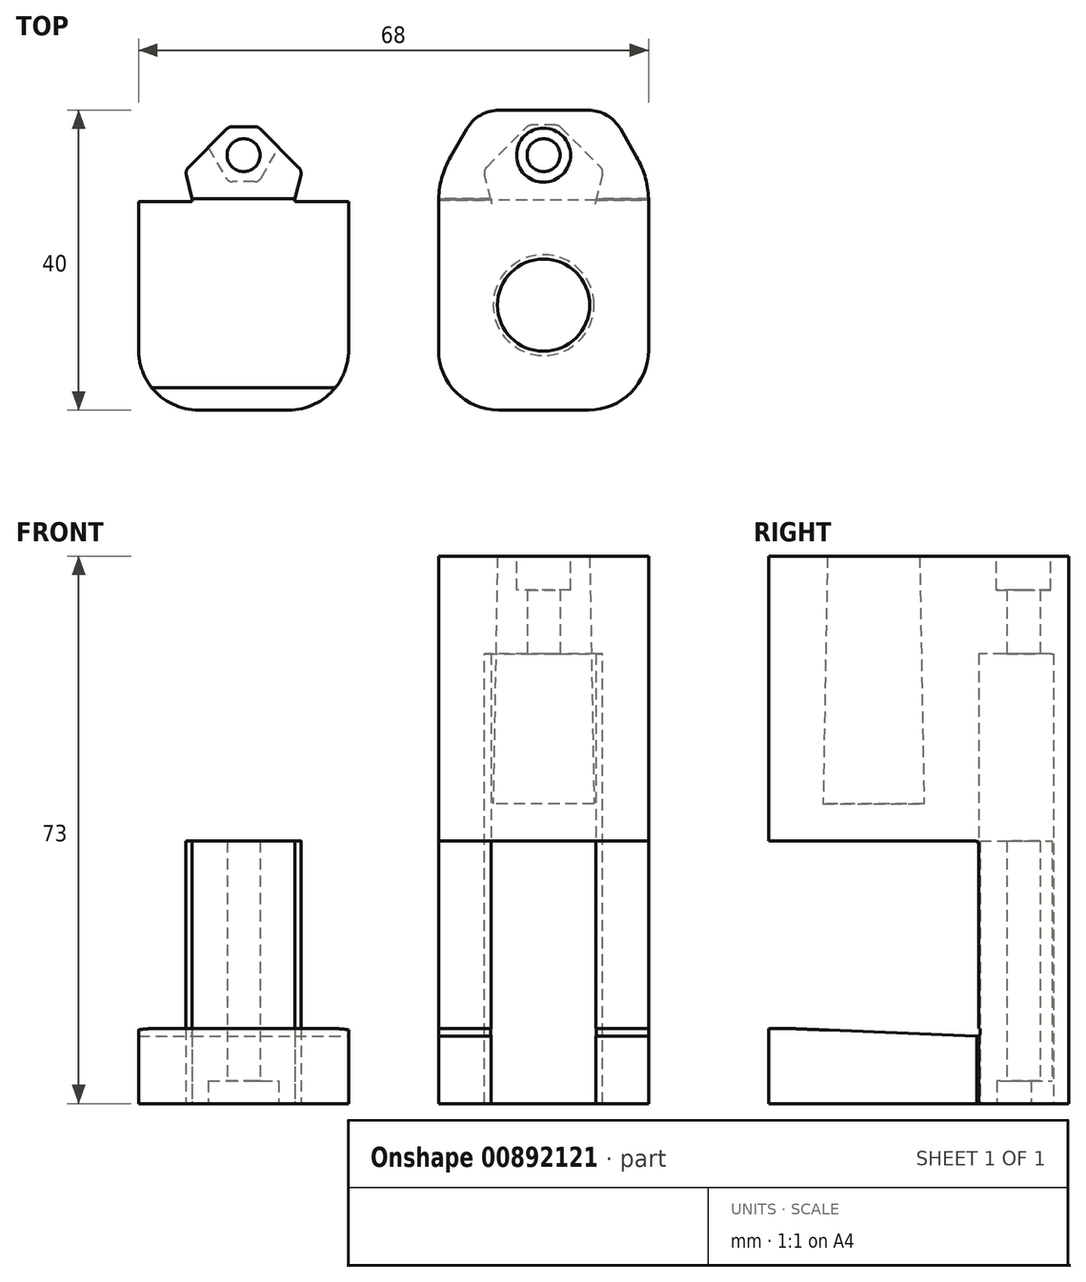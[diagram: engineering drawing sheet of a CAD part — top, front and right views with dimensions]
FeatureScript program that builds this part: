
annotation { "Feature Type Name" : "Feature", "Feature Type Description" : "" }
export const myFeature = defineFeature(function(context is Context, id is Id, definition is map)
    precondition{}
    {
        {
            assignVariable(context, id + "F0", {"name" : "lamppostDepth", "anyValue" : 33});
        }
        {
            var Q0;
            Q0=qCreatedBy(makeId("Right.planeOp"),FACE);
            var sketch = newSketch(context, id + "F1", { "sketchPlane" : qUnion([Q0])});
            skLineSegment(sketch, "E0", {"start": v(0, 0) * mm, "end": v(-28, 0) * mm});
            skLineSegment(sketch, "E1", {"start": v(-28, 0) * mm, "end": v(-28, 38) * mm});
            skLineSegment(sketch, "E2", {"start": v(-28, 38) * mm, "end": v(12, 38) * mm});
            skLineSegment(sketch, "E3", {"start": v(12, 38) * mm, "end": v(12, -35) * mm});
            skLineSegment(sketch, "E4", {"start": v(12, -35) * mm, "end": v(0, -35) * mm});
            skLineSegment(sketch, "E5", {"start": v(0, -35) * mm, "end": v(0, 0) * mm});
            skLineSegment(sketch, "E6", {"start": v(0, -25) * mm, "end": v(-22.92, -25) * mm, "construction": true});
            skSolve(sketch);
        }
        {
            var Q0;
            Q0=qSketchRegion(id+"F1",true);
            extrude(context, id + "F2", {"entities" : qUnion([Q0]), "endBound" : BoundingType.SYMMETRIC, "depth" : 28 * mm, "offsetDistance" : 25 * mm});
        }
        {
            var Q0;
            Q0=makeQuery(id+"F2.opExtrude","SWEPT_FACE",FACE,{"disambiguationData":[OSD([sQuery(id+"F1.wireOp",EDGE,"E2")])]});
            var sketch = newSketch(context, id + "F3", { "sketchPlane" : qUnion([Q0])});
            skCircle(sketch, "E7", {"center": v(0, -14) * mm, "radius": 6.15 * mm});
            skLineSegment(sketch, "E8", {"start": v(14, -28) * mm, "end": v(-14, 0) * mm, "construction": true});
            skLineSegment(sketch, "E9", {"start": v(-14, 0) * mm, "end": v(-14, -28) * mm, "construction": true});
            skSolve(sketch);
        }
        {
            var Q0;
            Q0=qSketchRegion(id+"F3",true);
            extrude(context, id + "F4", {"entities" : qUnion([Q0]), "operationType" : NewBodyOperationType.REMOVE, "oppositeDirection" : true, "depth" : (getVariable(context, 'lamppostDepth')) * mm, "offsetDistance" : 25 * mm, "hasDraft" : true, "draftAngle" : 1 * degree});
        }
        {
            var Q0;
            Q0=makeQuery(id+"F2.opExtrude","SWEPT_FACE",FACE,{"disambiguationData":[OSD([sQuery(id+"F1.wireOp",EDGE,"E4")])]});
            var sketch = newSketch(context, id + "F5", { "sketchPlane" : qUnion([Q0])});
            skCircle(sketch, "E10", {"center": v(0, -6) * mm, "radius": 2.2 * mm});
            skLineSegment(sketch, "E11", {"start": v(-14, -12) * mm, "end": v(14, 0) * mm, "construction": true});
            skSolve(sketch);
        }
        {
            var Q0;
            Q0=qSketchRegion(id+"F5",true);
            extrude(context, id + "F6", {"entities" : qUnion([Q0]), "operationType" : NewBodyOperationType.REMOVE, "endBound" : BoundingType.THROUGH_ALL, "oppositeDirection" : true, "depth" : 25 * mm, "offsetDistance" : 25 * mm});
        }
        {
            var Q0;
            Q0=makeQuery(id+"F2.opExtrude","SWEPT_FACE",FACE,{"disambiguationData":[OSD([sQuery(id+"F1.wireOp",EDGE,"E2")])]});
            var sketch = newSketch(context, id + "F7", { "sketchPlane" : qUnion([Q0])});
            skCircle(sketch, "E12", {"center": v(0, 6) * mm, "radius": 3.6 * mm});
            skSolve(sketch);
        }
        {
            var Q0;
            Q0=qSketchRegion(id+"F7",true);
            extrude(context, id + "F8", {"entities" : qUnion([Q0]), "operationType" : NewBodyOperationType.REMOVE, "oppositeDirection" : true, "depth" : 4.5 * mm, "offsetDistance" : 25 * mm});
        }
        {
            var Q0;
            Q0=makeQuery(id+"F2.opExtrude","SWEPT_FACE",FACE,{"disambiguationData":[OSD([sQuery(id+"F1.wireOp",EDGE,"E4")])]});
            var sketch = newSketch(context, id + "F9", { "sketchPlane" : qUnion([Q0])});
            skLineSegment(sketch, "E13", {"start": v(2, -10) * mm, "end": v(-2, -10) * mm});
            skPoint(sketch, "E14", {"position": v(0, -6) * mm});
            skLineSegment(sketch, "E15", {"start": v(0, -6) * mm, "end": v(0, -10) * mm, "construction": true});
            skLineSegment(sketch, "E16", {"start": v(2, -10) * mm, "end": v(8, -4) * mm});
            skLineSegment(sketch, "E17", {"start": v(8, -4) * mm, "end": v(7, 0) * mm});
            skLineSegment(sketch, "E18", {"start": v(7, 0) * mm, "end": v(-7, 0) * mm});
            skLineSegment(sketch, "E19", {"start": v(-7, 0) * mm, "end": v(-8, -4) * mm});
            skLineSegment(sketch, "E20", {"start": v(-8, -4) * mm, "end": v(-2, -10) * mm});
            skSolve(sketch);
        }
        {
            var Q0;
            Q0=qSketchRegion(id+"F9",true);
            extrude(context, id + "F10", {"entities" : qUnion([Q0]), "operationType" : NewBodyOperationType.REMOVE, "oppositeDirection" : true, "depth" : 60 * mm, "offsetDistance" : 25 * mm});
        }
        {
            var Q0;
            Q0=makeQuery(id+"F2.opExtrude","SWEPT_FACE",FACE,{"disambiguationData":[OSD([sQuery(id+"F1.wireOp",EDGE,"E4")])]});
            var sketch = newSketch(context, id + "F11", { "sketchPlane" : qUnion([Q0])});
            skLineSegment(sketch, "E21.0", {"start": v(7.78, -3.94) * mm, "end": v(6.84, -0.2) * mm});
            skLineSegment(sketch, "E21.1", {"start": v(-6.84, -0.2) * mm, "end": v(-7.78, -3.94) * mm});
            skLineSegment(sketch, "E21.2", {"start": v(-7.78, -3.94) * mm, "end": v(-1.92, -9.8) * mm});
            skLineSegment(sketch, "E21.3", {"start": v(1.92, -9.8) * mm, "end": v(-1.92, -9.8) * mm});
            skLineSegment(sketch, "E21.4", {"start": v(1.92, -9.8) * mm, "end": v(7.78, -3.94) * mm});
            skLineSegment(sketch, "E22", {"start": v(6.84, -0.2) * mm, "end": v(-6.84, -0.2) * mm});
            skCircle(sketch, "E23.0", {"center": v(0, -6) * mm, "radius": 2.2 * mm});
            skSolve(sketch);
        }
        {
            var Q0;
            Q0=qSketchRegion(id+"F11",true);
            extrude(context, id + "F12", {"entities" : qUnion([Q0]), "oppositeDirection" : true, "depth" : 35 * mm, "offsetDistance" : 25 * mm});
        }
        {
            var Q0;
            Q0=makeQuery(id+"F12.opExtrude","CAP_FACE",FACE,{"disambiguationData":[OSD([sQuery(id+"F11.wireOp",EDGE,"E21.0"),sQuery(id+"F11.wireOp",EDGE,"E21.1"),sQuery(id+"F11.wireOp",EDGE,"E21.2"),sQuery(id+"F11.wireOp",EDGE,"E21.3"),sQuery(id+"F11.wireOp",EDGE,"E21.4"),sQuery(id+"F11.wireOp",EDGE,"E22"),sQuery(id+"F11.wireOp",EDGE,"E23.0")])],"isStart":true});
            var sketch = newSketch(context, id + "F13", { "sketchPlane" : qUnion([Q0])});
            skLineSegment(sketch, "E24", {"start": v(14, 28) * mm, "end": v(-14, 28) * mm});
            skLineSegment(sketch, "E25", {"start": v(-14, 28) * mm, "end": v(-14, 0.2) * mm});
            skLineSegment(sketch, "E26", {"start": v(-14, 0.2) * mm, "end": v(-6.84, 0.2) * mm});
            skLineSegment(sketch, "E27", {"start": v(-6.84, 0.2) * mm, "end": v(-6.84, -0.2) * mm});
            skLineSegment(sketch, "E28", {"start": v(-6.84, -0.2) * mm, "end": v(6.84, -0.2) * mm});
            skLineSegment(sketch, "E29", {"start": v(6.84, -0.2) * mm, "end": v(6.84, 0.2) * mm});
            skLineSegment(sketch, "E30", {"start": v(6.84, 0.2) * mm, "end": v(14, 0.2) * mm});
            skLineSegment(sketch, "E31", {"start": v(14, 0.2) * mm, "end": v(14, 28) * mm});
            skSolve(sketch);
        }
        {
            var Q0;
            Q0=makeQuery(id+"F13.imprint","IMPRINT",FACE,{"disambiguationData":[TD([[makeQuery(id+"F13.imprint","IMPRINT",EDGE,{"derivedFrom":sQuery(id+"F13.wireOp",EDGE,"E24")}),1.0]])]});
            var Q1;
            Q1=sQuery(id+"F1.wireOp",VERTEX,"E6.end");
            extrude(context, id + "F14", {"entities" : qUnion([Q0]), "operationType" : NewBodyOperationType.ADD, "endBound" : BoundingType.UP_TO_VERTEX, "oppositeDirection" : true, "depth" : 10 * mm, "endBoundEntityVertex" : qUnion([Q1]), "offsetDistance" : 25 * mm});
        }
        {
            var Q0;
            Q0=makeQuery(id+"F14.boolean.opBoolean","MERGE",FACE,{"derivedFrom":[makeQuery(id+"F12.opExtrude","CAP_FACE",FACE,{"disambiguationData":[OSD([sQuery(id+"F11.wireOp",EDGE,"E21.0"),sQuery(id+"F11.wireOp",EDGE,"E21.1"),sQuery(id+"F11.wireOp",EDGE,"E21.2"),sQuery(id+"F11.wireOp",EDGE,"E21.3"),sQuery(id+"F11.wireOp",EDGE,"E21.4"),sQuery(id+"F11.wireOp",EDGE,"E22"),sQuery(id+"F11.wireOp",EDGE,"E23.0")])],"isStart":true}),makeQuery(id+"F14.opExtrude","CAP_FACE",FACE,{"disambiguationData":[OSD([sQuery(id+"F13.wireOp",EDGE,"E24"),sQuery(id+"F13.wireOp",EDGE,"E25"),sQuery(id+"F13.wireOp",EDGE,"E26"),sQuery(id+"F13.wireOp",EDGE,"E27"),sQuery(id+"F13.wireOp",EDGE,"E28"),sQuery(id+"F13.wireOp",EDGE,"E29"),sQuery(id+"F13.wireOp",EDGE,"E30"),sQuery(id+"F13.wireOp",EDGE,"E31")])],"isStart":true})]});
            var sketch = newSketch(context, id + "F15", { "sketchPlane" : qUnion([Q0])});
            skCircle(sketch, "E32", {"center": v(0, -6) * mm, "radius": 4.1 * mm, "construction": true});
            skLineSegment(sketch, "E33", {"start": v(2.05, -2.45) * mm, "end": v(-2.05, -2.45) * mm});
            skLineSegment(sketch, "E34", {"start": v(2.05, -2.45) * mm, "end": v(4.1, -6) * mm});
            skLineSegment(sketch, "E35", {"start": v(4.1, -6) * mm, "end": v(0, -6) * mm, "construction": true});
            skLineSegment(sketch, "E36", {"start": v(0, -6) * mm, "end": v(-4.1, -6) * mm, "construction": true});
            skLineSegment(sketch, "E37", {"start": v(-4.1, -6) * mm, "end": v(-2.05, -2.45) * mm});
            skLineSegment(sketch, "E38", {"start": v(4.1, -6) * mm, "end": v(4.7, -7.03) * mm});
            skLineSegment(sketch, "E39", {"start": v(4.7, -7.03) * mm, "end": v(1.92, -9.8) * mm});
            skLineSegment(sketch, "E40", {"start": v(1.92, -9.8) * mm, "end": v(-1.92, -9.8) * mm});
            skLineSegment(sketch, "E41", {"start": v(-1.92, -9.8) * mm, "end": v(-4.7, -7.03) * mm});
            skLineSegment(sketch, "E42", {"start": v(-4.7, -7.03) * mm, "end": v(-4.1, -6) * mm});
            skSolve(sketch);
        }
        {
            var Q0;
            Q0=qSketchRegion(id+"F15",true);
            extrude(context, id + "F16", {"entities" : qUnion([Q0]), "operationType" : NewBodyOperationType.REMOVE, "oppositeDirection" : true, "depth" : 3 * mm, "offsetDistance" : 25 * mm});
        }
        {
            var Q0;
            Q0=makeQuery(id+"F2.opExtrude","CAP_EDGE",EDGE,{"disambiguationData":[OSD([sQuery(id+"F1.wireOp",EDGE,"E1")])],"isStart":false});
            var Q1;
            Q1=makeQuery(id+"F2.opExtrude","CAP_EDGE",EDGE,{"disambiguationData":[OSD([sQuery(id+"F1.wireOp",EDGE,"E1")])],"isStart":true});
            var Q2;
            Q2=makeQuery(id+"F14.opExtrude","SWEPT_EDGE",EDGE,{"disambiguationData":[OSD([sQuery(id+"F13.wireOp",EDGE,"E24"),sQuery(id+"F13.wireOp",EDGE,"E31")])]});
            var Q3;
            Q3=makeQuery(id+"F14.opExtrude","SWEPT_EDGE",EDGE,{"disambiguationData":[OSD([sQuery(id+"F13.wireOp",EDGE,"E24"),sQuery(id+"F13.wireOp",EDGE,"E25")])]});
            fillet(context, id + "F17", {"entities" : qUnion([Q0, Q1, Q2, Q3]), "radius" : 8 * mm, "tangentPropagation" : true, "allowEdgeOverflow" : false});
        }
        {
            var Q0;
            Q0=makeQuery(id+"F2.opExtrude","CAP_EDGE",EDGE,{"disambiguationData":[OSD([sQuery(id+"F1.wireOp",EDGE,"E3")])],"isStart":true});
            var Q1;
            Q1=makeQuery(id+"F2.opExtrude","CAP_EDGE",EDGE,{"disambiguationData":[OSD([sQuery(id+"F1.wireOp",EDGE,"E3")])],"isStart":false});
            chamfer(context, id + "F18", {"entities" : qUnion([Q0, Q1]), "chamferType" : ChamferType.OFFSET_ANGLE, "width" : 9 * mm, "oppositeDirection" : false, "angle" : 30 * degree, "tangentPropagation" : true});
        }
        {
            var Q0;
            {var subQ0=sQuery(id+"F1.wireOp",EDGE,"E3");Q0=makeQuery(id+"F18.opChamfer","BLEND_EDGE",EDGE,{"blendedFrom":[makeQuery(id+"F2.opExtrude","CAP_EDGE",EDGE,{"disambiguationData":[OSD([subQ0])],"isStart":true}),makeQuery(id+"F2.opExtrude","CAP_FACE",FACE,{"disambiguationData":[OSD([sQuery(id+"F1.wireOp",EDGE,"E0"),sQuery(id+"F1.wireOp",EDGE,"E1"),sQuery(id+"F1.wireOp",EDGE,"E2"),subQ0,sQuery(id+"F1.wireOp",EDGE,"E4"),sQuery(id+"F1.wireOp",EDGE,"E5")])],"isStart":true})],"blendedInto":[makeQuery(id+"F2.opExtrude","CAP_FACE",FACE,{"disambiguationData":[OSD([sQuery(id+"F1.wireOp",EDGE,"E0"),sQuery(id+"F1.wireOp",EDGE,"E1"),sQuery(id+"F1.wireOp",EDGE,"E2"),subQ0,sQuery(id+"F1.wireOp",EDGE,"E4"),sQuery(id+"F1.wireOp",EDGE,"E5")])],"isStart":true})]});}
            var Q1;
            {var subQ0=sQuery(id+"F1.wireOp",EDGE,"E3");Q1=makeQuery(id+"F18.opChamfer","BLEND_EDGE",EDGE,{"blendedFrom":[makeQuery(id+"F2.opExtrude","CAP_EDGE",EDGE,{"disambiguationData":[OSD([subQ0])],"isStart":false}),makeQuery(id+"F2.opExtrude","CAP_FACE",FACE,{"disambiguationData":[OSD([sQuery(id+"F1.wireOp",EDGE,"E0"),sQuery(id+"F1.wireOp",EDGE,"E1"),sQuery(id+"F1.wireOp",EDGE,"E2"),subQ0,sQuery(id+"F1.wireOp",EDGE,"E4"),sQuery(id+"F1.wireOp",EDGE,"E5")])],"isStart":false})],"blendedInto":[makeQuery(id+"F2.opExtrude","CAP_FACE",FACE,{"disambiguationData":[OSD([sQuery(id+"F1.wireOp",EDGE,"E0"),sQuery(id+"F1.wireOp",EDGE,"E1"),sQuery(id+"F1.wireOp",EDGE,"E2"),subQ0,sQuery(id+"F1.wireOp",EDGE,"E4"),sQuery(id+"F1.wireOp",EDGE,"E5")])],"isStart":false})]});}
            fillet(context, id + "F19", {"entities" : qUnion([Q0, Q1]), "radius" : 12 * mm, "tangentPropagation" : true, "allowEdgeOverflow" : false});
        }
        {
            var Q0;
            {var subQ0=sQuery(id+"F1.wireOp",EDGE,"E3");Q0=makeQuery(id+"F18.opChamfer","BLEND_EDGE",EDGE,{"blendedFrom":[makeQuery(id+"F2.opExtrude","CAP_EDGE",EDGE,{"disambiguationData":[OSD([subQ0])],"isStart":true}),makeQuery(id+"F2.opExtrude","SWEPT_FACE",FACE,{"disambiguationData":[OSD([subQ0])]})],"blendedInto":[makeQuery(id+"F2.opExtrude","SWEPT_FACE",FACE,{"disambiguationData":[OSD([subQ0])]})]});}
            var Q1;
            {var subQ0=sQuery(id+"F1.wireOp",EDGE,"E3");Q1=makeQuery(id+"F18.opChamfer","BLEND_EDGE",EDGE,{"blendedFrom":[makeQuery(id+"F2.opExtrude","CAP_EDGE",EDGE,{"disambiguationData":[OSD([subQ0])],"isStart":false}),makeQuery(id+"F2.opExtrude","SWEPT_FACE",FACE,{"disambiguationData":[OSD([subQ0])]})],"blendedInto":[makeQuery(id+"F2.opExtrude","SWEPT_FACE",FACE,{"disambiguationData":[OSD([subQ0])]})]});}
            fillet(context, id + "F20", {"entities" : qUnion([Q0, Q1]), "radius" : 5 * mm, "tangentPropagation" : true, "allowEdgeOverflow" : false});
        }
        {
            var Q0;
            Q0=makeQuery(id+"F14.opExtrude","SWEPT_FACE",FACE,{"disambiguationData":[OSD([sQuery(id+"F13.wireOp",EDGE,"E25")])]});
            var sketch = newSketch(context, id + "F21", { "sketchPlane" : qUnion([Q0])});
            skLineSegment(sketch, "E43", {"start": v(-0.2, -25) * mm, "end": v(25, -25) * mm});
            skLineSegment(sketch, "E44", {"start": v(25, -25) * mm, "end": v(-0.2, -26) * mm});
            skLineSegment(sketch, "E45", {"start": v(-0.2, -26) * mm, "end": v(-0.2, -25) * mm});
            skSolve(sketch);
        }
        {
            var Q0;
            Q0=qSketchRegion(id+"F21",true);
            extrude(context, id + "F22", {"entities" : qUnion([Q0]), "operationType" : NewBodyOperationType.REMOVE, "endBound" : BoundingType.THROUGH_ALL, "oppositeDirection" : true, "depth" : 25 * mm, "offsetDistance" : 25 * mm});
        }
        {
            var Q0;
            Q0=makeQuery(id+"F14.opExtrude","CAP_EDGE",EDGE,{"disambiguationData":[OSD([sQuery(id+"F13.wireOp",EDGE,"E28")])],"isStart":false});
            var Q1;
            {var subQ0=sQuery(id+"F1.wireOp",EDGE,"E5");var subQ1=makeQuery(id+"F2.opExtrude","SWEPT_FACE",FACE,{"disambiguationData":[OSD([subQ0])]});var subQ2=sQuery(id+"F1.wireOp",EDGE,"E0");var subQ3=makeQuery(id+"F2.opExtrude","SWEPT_FACE",FACE,{"disambiguationData":[OSD([subQ2])]});Q1=makeQuery(id+"F10.boolean.opBoolean","SPLIT",EDGE,{"disambiguationData":[topologyDisambiguationEdgeConnected([subQ3,subQ1]),TD([makeQuery(id+"F10.opExtrude","SWEPT_FACE",FACE,{"disambiguationData":[OSD([sQuery(id+"F9.wireOp",EDGE,"E17")])]})])],"derivedFrom":makeQuery(id+"F2.opExtrude","SWEPT_EDGE",EDGE,{"disambiguationData":[OSD([subQ2,subQ0])]})});}
            var Q2;
            {var subQ0=sQuery(id+"F1.wireOp",EDGE,"E5");var subQ1=makeQuery(id+"F2.opExtrude","SWEPT_FACE",FACE,{"disambiguationData":[OSD([subQ0])]});var subQ2=sQuery(id+"F1.wireOp",EDGE,"E0");var subQ3=makeQuery(id+"F2.opExtrude","SWEPT_FACE",FACE,{"disambiguationData":[OSD([subQ2])]});Q2=makeQuery(id+"F10.boolean.opBoolean","SPLIT",EDGE,{"disambiguationData":[topologyDisambiguationEdgeConnected([subQ3,subQ1]),TD([makeQuery(id+"F10.opExtrude","SWEPT_FACE",FACE,{"disambiguationData":[OSD([sQuery(id+"F9.wireOp",EDGE,"E19")])]})])],"derivedFrom":makeQuery(id+"F2.opExtrude","SWEPT_EDGE",EDGE,{"disambiguationData":[OSD([subQ2,subQ0])]})});}
            var Q3;
            Q3=makeQuery(id+"F22.boolean.opBoolean","COPY",EDGE,{"derivedFrom":makeQuery(id+"F22.opExtrude","SWEPT_EDGE",EDGE,{"disambiguationData":[OSD([sQuery(id+"F21.wireOp",EDGE,"E44"),sQuery(id+"F21.wireOp",EDGE,"E45")])]})});
            fillet(context, id + "F23", {"entities" : qUnion([Q0, Q1, Q2, Q3]), "radius" : .5 * mm, "tangentPropagation" : true, "rho" : .7, "crossSection" : FilletCrossSection.CONIC, "allowEdgeOverflow" : false});
        }
        {
            var Q0;
            Q0=makeQuery(id+"F10.boolean.opBoolean","COPY",EDGE,{"derivedFrom":makeQuery(id+"F10.opExtrude","SWEPT_EDGE",EDGE,{"disambiguationData":[OSD([sQuery(id+"F9.wireOp",EDGE,"E19"),sQuery(id+"F9.wireOp",EDGE,"E20")])]})});
            var Q1;
            Q1=makeQuery(id+"F12.opExtrude","SWEPT_EDGE",EDGE,{"disambiguationData":[OSD([sQuery(id+"F11.wireOp",EDGE,"E21.1"),sQuery(id+"F11.wireOp",EDGE,"E21.2")])]});
            var Q2;
            Q2=makeQuery(id+"F16.boolean.opBoolean","COPY",EDGE,{"derivedFrom":makeQuery(id+"F16.opExtrude","SWEPT_EDGE",EDGE,{"disambiguationData":[OSD([sQuery(id+"F15.wireOp",EDGE,"E33"),sQuery(id+"F15.wireOp",EDGE,"E37")])]})});
            var Q3;
            Q3=makeQuery(id+"F16.boolean.opBoolean","COPY",EDGE,{"derivedFrom":makeQuery(id+"F16.opExtrude","SWEPT_EDGE",EDGE,{"disambiguationData":[OSD([sQuery(id+"F15.wireOp",EDGE,"E33"),sQuery(id+"F15.wireOp",EDGE,"E34")])]})});
            var Q4;
            Q4=makeQuery(id+"F10.boolean.opBoolean","COPY",EDGE,{"derivedFrom":makeQuery(id+"F10.opExtrude","SWEPT_EDGE",EDGE,{"disambiguationData":[OSD([sQuery(id+"F9.wireOp",EDGE,"E13"),sQuery(id+"F9.wireOp",EDGE,"E20")])]})});
            var Q5;
            Q5=makeQuery(id+"F10.boolean.opBoolean","COPY",EDGE,{"derivedFrom":makeQuery(id+"F10.opExtrude","SWEPT_EDGE",EDGE,{"disambiguationData":[OSD([sQuery(id+"F9.wireOp",EDGE,"E13"),sQuery(id+"F9.wireOp",EDGE,"E16")])]})});
            var Q6;
            Q6=makeQuery(id+"F10.boolean.opBoolean","COPY",EDGE,{"derivedFrom":makeQuery(id+"F10.opExtrude","SWEPT_EDGE",EDGE,{"disambiguationData":[OSD([sQuery(id+"F9.wireOp",EDGE,"E16"),sQuery(id+"F9.wireOp",EDGE,"E17")])]})});
            var Q7;
            Q7=makeQuery(id+"F12.opExtrude","SWEPT_EDGE",EDGE,{"disambiguationData":[OSD([sQuery(id+"F11.wireOp",EDGE,"E21.0"),sQuery(id+"F11.wireOp",EDGE,"E21.4")])]});
            var Q8;
            Q8=makeQuery(id+"F12.opExtrude","SWEPT_EDGE",EDGE,{"disambiguationData":[OSD([sQuery(id+"F11.wireOp",EDGE,"E21.3"),sQuery(id+"F11.wireOp",EDGE,"E21.4")])]});
            var Q9;
            Q9=makeQuery(id+"F12.opExtrude","SWEPT_EDGE",EDGE,{"disambiguationData":[OSD([sQuery(id+"F11.wireOp",EDGE,"E21.2"),sQuery(id+"F11.wireOp",EDGE,"E21.3")])]});
            fillet(context, id + "F24", {"entities" : qUnion([Q0, Q1, Q2, Q3, Q4, Q5, Q6, Q7, Q8, Q9]), "radius" : 1 * mm, "tangentPropagation" : true, "allowEdgeOverflow" : false});
        }
        {
            var Q0;
            Q0=makeQuery(id+"F12.opExtrude","SWEPT_BODY",BODY,{"disambiguationData":[OSD([sQuery(id+"F11.wireOp",EDGE,"E21.0"),sQuery(id+"F11.wireOp",EDGE,"E21.1"),sQuery(id+"F11.wireOp",EDGE,"E21.2"),sQuery(id+"F11.wireOp",EDGE,"E21.3"),sQuery(id+"F11.wireOp",EDGE,"E21.4"),sQuery(id+"F11.wireOp",EDGE,"E22"),sQuery(id+"F11.wireOp",EDGE,"E23.0")])]});
            var Q1;
            {var subQ0=sQuery(id+"F1.wireOp",EDGE,"E5");var subQ1=sQuery(id+"F1.wireOp",EDGE,"E4");Q1=makeQuery(id+"F10.boolean.opBoolean","SPLIT",EDGE,{"disambiguationData":[TD([makeQuery(id+"F10.opExtrude","SWEPT_FACE",FACE,{"disambiguationData":[OSD([sQuery(id+"F9.wireOp",EDGE,"E17")])]})])],"derivedFrom":makeQuery(id+"F2.opExtrude","SWEPT_EDGE",EDGE,{"disambiguationData":[OSD([subQ1,subQ0])]})});}
            var Q2;
            {var subQ0=sQuery(id+"F1.wireOp",EDGE,"E5");var subQ1=sQuery(id+"F1.wireOp",EDGE,"E4");Q2=makeQuery(id+"F10.boolean.opBoolean","SPLIT",EDGE,{"disambiguationData":[TD([makeQuery(id+"F10.opExtrude","SWEPT_FACE",FACE,{"disambiguationData":[OSD([sQuery(id+"F9.wireOp",EDGE,"E19")])]})])],"derivedFrom":makeQuery(id+"F2.opExtrude","SWEPT_EDGE",EDGE,{"disambiguationData":[OSD([subQ1,subQ0])]})});}
            transform(context, id + "F25", {"entities" : qUnion([Q0]), "transformType" : TransformType.TRANSLATION_DISTANCE, "transformDirection" : qUnion([Q2]), "distance" : 40 * mm, "makeCopy" : false});
        }
    });
